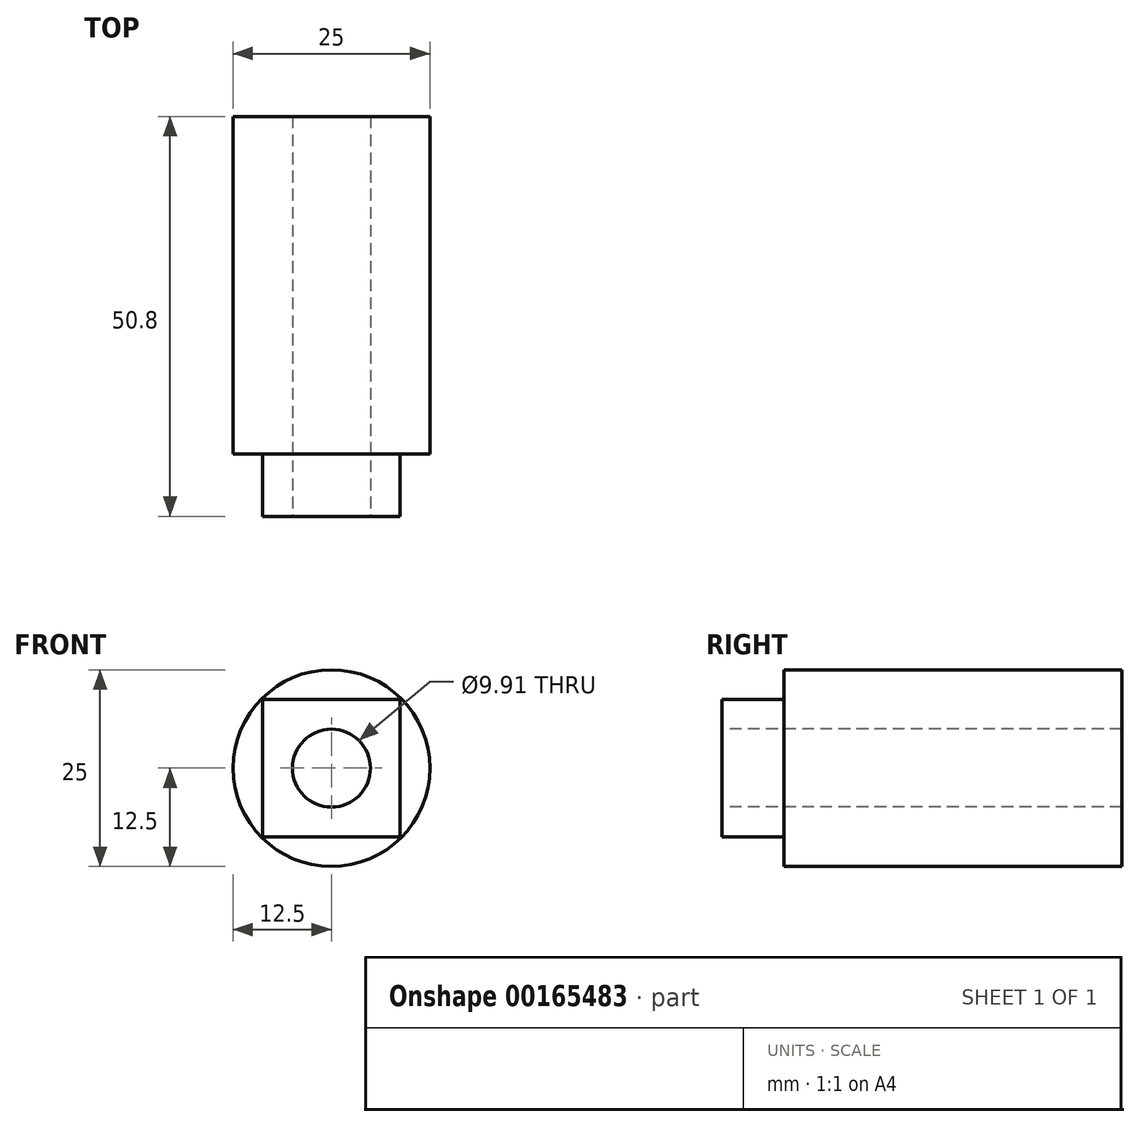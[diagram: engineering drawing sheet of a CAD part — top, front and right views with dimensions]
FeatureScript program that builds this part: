
annotation { "Feature Type Name" : "Feature", "Feature Type Description" : "" }
export const myFeature = defineFeature(function(context is Context, id is Id, definition is map)
    precondition{}
    {
        {
            var Q0;
            Q0=qCreatedBy(makeId("Front.planeOp"),FACE);
            var sketch = newSketch(context, id + "F0", { "sketchPlane" : qUnion([Q0])});
            skCircle(sketch, "E0", {"center": v(0, 0) * mm, "radius": 12.5 * mm});
            skSolve(sketch);
        }
        {
            var Q0;
            Q0 = qSketchRegion(id + "F0", true);
            extrude(context, id + "F1", {"entities" : qUnion([Q0]), "oppositeDirection" : true, "depth" : 42.9 * mm});
        }
        {
            var Q0;
            Q0=makeQuery(id+"F1.opExtrude","CAP_FACE",FACE,{"disambiguationData":[OSD([sQuery(id+"F0.wireOp",EDGE,"E0")])],"isStart":true});
            var sketch = newSketch(context, id + "F2", { "sketchPlane" : qUnion([Q0])});
            skLineSegment(sketch, "E1.bottom", {"start": v(8.72, 8.72) * mm, "end": v(-8.72, 8.72) * mm});
            skLineSegment(sketch, "E1.top", {"start": v(8.72, -8.72) * mm, "end": v(-8.72, -8.72) * mm});
            skLineSegment(sketch, "E1.left", {"start": v(8.72, 8.72) * mm, "end": v(8.72, -8.72) * mm});
            skLineSegment(sketch, "E1.right", {"start": v(-8.72, 8.72) * mm, "end": v(-8.72, -8.72) * mm});
            skPoint(sketch, "E1.middle", {"position": v(0, 0) * mm});
            skSolve(sketch);
        }
        {
            var Q0;
            Q0 = qSketchRegion(id + "F2", true);
            extrude(context, id + "F3", {"entities" : qUnion([Q0]), "operationType" : NewBodyOperationType.ADD, "depth" : 7.9 * mm});
        }
        {
            var Q0;
            Q0=makeQuery(id+"F3.opExtrude","CAP_FACE",FACE,{"disambiguationData":[OSD([sQuery(id+"F2.wireOp",EDGE,"E1.bottom"),sQuery(id+"F2.wireOp",EDGE,"E1.top"),sQuery(id+"F2.wireOp",EDGE,"E1.left"),sQuery(id+"F2.wireOp",EDGE,"E1.right")])],"isStart":false});
            var sketch = newSketch(context, id + "F4", { "sketchPlane" : qUnion([Q0])});
            skCircle(sketch, "E2", {"center": v(0, 0) * mm, "radius": 4.95 * mm});
            skSolve(sketch);
        }
        {
            var Q0;
            Q0 = qSketchRegion(id + "F4", true);
            extrude(context, id + "F5", {"entities" : qUnion([Q0]), "operationType" : NewBodyOperationType.REMOVE, "oppositeDirection" : true, "depth" : 50.8 * mm});
        }
    });
